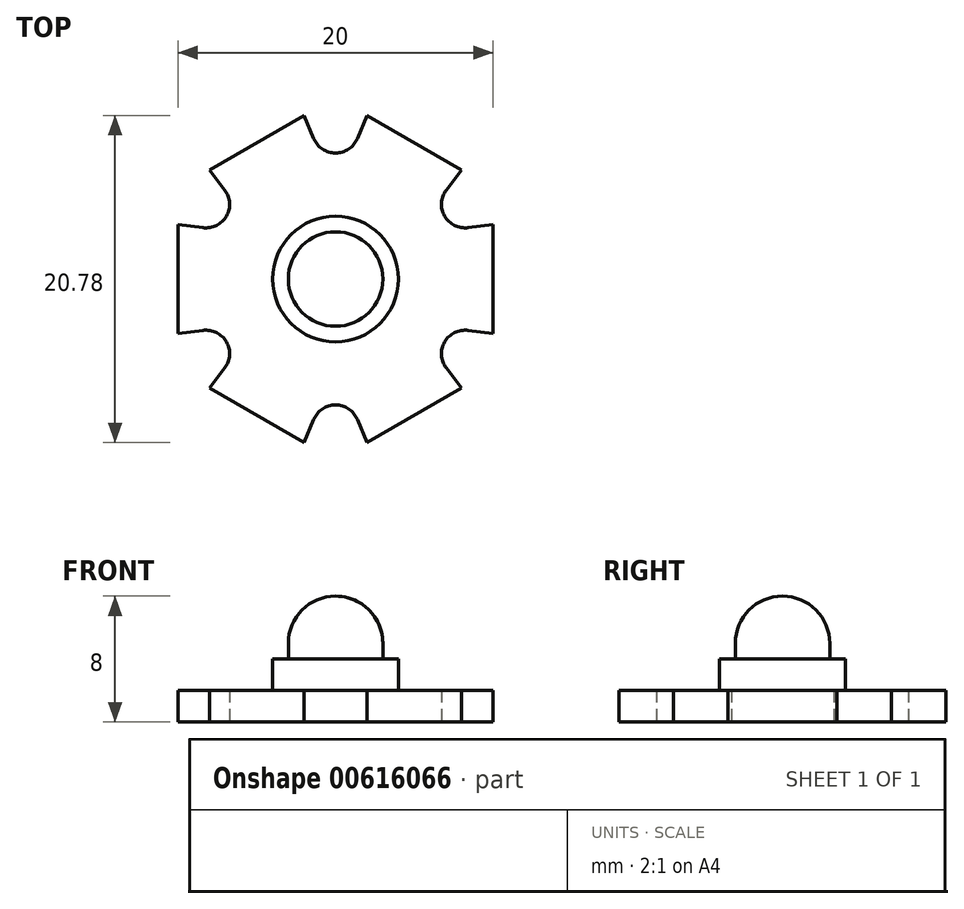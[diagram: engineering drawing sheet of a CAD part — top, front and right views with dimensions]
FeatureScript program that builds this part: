
annotation { "Feature Type Name" : "Feature", "Feature Type Description" : "" }
export const myFeature = defineFeature(function(context is Context, id is Id, definition is map)
    precondition{}
    {
        {
            var Q0;
            Q0=qCreatedBy(makeId("Top.planeOp"),FACE);
            var sketch = newSketch(context, id + "F0", { "sketchPlane" : qUnion([Q0])});
            skArc(sketch, "E0", {"start": v(0, -8) * mm, "mid": v(-0.83, -8.25) * mm, "end": v(-1.38, -8.92) * mm});
            skLineSegment(sketch, "E1", {"start": v(-1.38, -8.92) * mm, "end": v(-2, -10.4) * mm});
            skLineSegment(sketch, "E2", {"start": v(-2, -10.4) * mm, "end": v(-8, -6.93) * mm});
            skArc(sketch, "E3.MirrorCS", {"start": v(0, -8) * mm, "mid": v(0.83, -8.25) * mm, "end": v(1.38, -8.92) * mm});
            skLineSegment(sketch, "E4.MirrorCS", {"start": v(1.38, -8.92) * mm, "end": v(2, -10.4) * mm});
            skLineSegment(sketch, "E5.1.0", {"start": v(8, -6.93) * mm, "end": v(2, -10.4) * mm});
            skLineSegment(sketch, "E5.1.1", {"start": v(7.03, -5.66) * mm, "end": v(8, -6.93) * mm});
            skArc(sketch, "E5.1.2", {"start": v(6.93, -4) * mm, "mid": v(6.73, -4.85) * mm, "end": v(7.03, -5.66) * mm});
            skArc(sketch, "E5.1.3", {"start": v(6.93, -4) * mm, "mid": v(7.56, -3.4) * mm, "end": v(8.42, -3.26) * mm});
            skLineSegment(sketch, "E5.1.4", {"start": v(8.42, -3.26) * mm, "end": v(10, -3.46) * mm});
            skLineSegment(sketch, "E5.2.0", {"start": v(10, 3.46) * mm, "end": v(10, -3.46) * mm});
            skLineSegment(sketch, "E5.2.1", {"start": v(8.42, 3.26) * mm, "end": v(10, 3.46) * mm});
            skArc(sketch, "E5.2.2", {"start": v(6.93, 4) * mm, "mid": v(7.56, 3.4) * mm, "end": v(8.42, 3.26) * mm});
            skArc(sketch, "E5.2.3", {"start": v(6.93, 4) * mm, "mid": v(6.73, 4.85) * mm, "end": v(7.03, 5.66) * mm});
            skLineSegment(sketch, "E5.2.4", {"start": v(7.03, 5.66) * mm, "end": v(8, 6.93) * mm});
            skLineSegment(sketch, "E5.3.0", {"start": v(2, 10.4) * mm, "end": v(8, 6.93) * mm});
            skLineSegment(sketch, "E5.3.1", {"start": v(1.38, 8.92) * mm, "end": v(2, 10.4) * mm});
            skArc(sketch, "E5.3.2", {"start": v(0, 8) * mm, "mid": v(0.83, 8.25) * mm, "end": v(1.38, 8.92) * mm});
            skArc(sketch, "E5.3.3", {"start": v(0, 8) * mm, "mid": v(-0.83, 8.25) * mm, "end": v(-1.38, 8.92) * mm});
            skLineSegment(sketch, "E5.3.4", {"start": v(-1.38, 8.92) * mm, "end": v(-2, 10.4) * mm});
            skLineSegment(sketch, "E5.4.0", {"start": v(-8, 6.93) * mm, "end": v(-2, 10.4) * mm});
            skLineSegment(sketch, "E5.4.1", {"start": v(-7.03, 5.66) * mm, "end": v(-8, 6.93) * mm});
            skArc(sketch, "E5.4.2", {"start": v(-6.93, 4) * mm, "mid": v(-6.73, 4.85) * mm, "end": v(-7.03, 5.66) * mm});
            skArc(sketch, "E5.4.3", {"start": v(-6.93, 4) * mm, "mid": v(-7.56, 3.4) * mm, "end": v(-8.42, 3.26) * mm});
            skLineSegment(sketch, "E5.4.4", {"start": v(-8.42, 3.26) * mm, "end": v(-10, 3.46) * mm});
            skLineSegment(sketch, "E5.5.0", {"start": v(-10, -3.46) * mm, "end": v(-10, 3.46) * mm});
            skLineSegment(sketch, "E5.5.1", {"start": v(-8.42, -3.26) * mm, "end": v(-10, -3.46) * mm});
            skArc(sketch, "E5.5.2", {"start": v(-6.93, -4) * mm, "mid": v(-7.56, -3.4) * mm, "end": v(-8.42, -3.26) * mm});
            skArc(sketch, "E5.5.3", {"start": v(-6.93, -4) * mm, "mid": v(-6.73, -4.85) * mm, "end": v(-7.03, -5.66) * mm});
            skLineSegment(sketch, "E5.5.4", {"start": v(-7.03, -5.66) * mm, "end": v(-8, -6.93) * mm});
            skPoint(sketch, "E5.center", {"position": v(0, 0) * mm});
            skSolve(sketch);
        }
        {
            var Q0;
            Q0=makeQuery(id+"F0.imprint","IMPRINT",FACE,{"disambiguationData":[TD([[makeQuery(id+"F0.imprint","IMPRINT",EDGE,{"derivedFrom":sQuery(id+"F0.wireOp",EDGE,"E0")}),-1.0]])]});
            extrude(context, id + "F1", {"entities" : qUnion([Q0]), "depth" : 2 * mm, "offsetDistance" : 25 * mm});
        }
        {
            var Q0;
            Q0=makeQuery(id+"F1.opExtrude","CAP_FACE",FACE,{"disambiguationData":[OSD([sQuery(id+"F0.wireOp",EDGE,"E0"),sQuery(id+"F0.wireOp",EDGE,"E1"),sQuery(id+"F0.wireOp",EDGE,"E2"),sQuery(id+"F0.wireOp",EDGE,"E3.MirrorCS"),sQuery(id+"F0.wireOp",EDGE,"E4.MirrorCS"),sQuery(id+"F0.wireOp",EDGE,"E5.1.0"),sQuery(id+"F0.wireOp",EDGE,"E5.1.1"),sQuery(id+"F0.wireOp",EDGE,"E5.1.2"),sQuery(id+"F0.wireOp",EDGE,"E5.1.3"),sQuery(id+"F0.wireOp",EDGE,"E5.1.4"),sQuery(id+"F0.wireOp",EDGE,"E5.2.0"),sQuery(id+"F0.wireOp",EDGE,"E5.2.1"),sQuery(id+"F0.wireOp",EDGE,"E5.2.2"),sQuery(id+"F0.wireOp",EDGE,"E5.2.3"),sQuery(id+"F0.wireOp",EDGE,"E5.2.4"),sQuery(id+"F0.wireOp",EDGE,"E5.3.0"),sQuery(id+"F0.wireOp",EDGE,"E5.3.1"),sQuery(id+"F0.wireOp",EDGE,"E5.3.2"),sQuery(id+"F0.wireOp",EDGE,"E5.3.3"),sQuery(id+"F0.wireOp",EDGE,"E5.3.4"),sQuery(id+"F0.wireOp",EDGE,"E5.4.0"),sQuery(id+"F0.wireOp",EDGE,"E5.4.1"),sQuery(id+"F0.wireOp",EDGE,"E5.4.2"),sQuery(id+"F0.wireOp",EDGE,"E5.4.3"),sQuery(id+"F0.wireOp",EDGE,"E5.4.4"),sQuery(id+"F0.wireOp",EDGE,"E5.5.0"),sQuery(id+"F0.wireOp",EDGE,"E5.5.1"),sQuery(id+"F0.wireOp",EDGE,"E5.5.2"),sQuery(id+"F0.wireOp",EDGE,"E5.5.3"),sQuery(id+"F0.wireOp",EDGE,"E5.5.4")])],"isStart":false});
            var sketch = newSketch(context, id + "F2", { "sketchPlane" : qUnion([Q0])});
            skCircle(sketch, "E6", {"center": v(0, 0) * mm, "radius": 4 * mm});
            skSolve(sketch);
        }
        {
            var Q0;
            Q0 = qSketchRegion(id + "F2", true);
            extrude(context, id + "F3", {"entities" : qUnion([Q0]), "operationType" : NewBodyOperationType.ADD, "depth" : 2 * mm, "offsetDistance" : 25 * mm});
        }
        {
            var Q0;
            Q0=qCreatedBy(makeId("Front.planeOp"),FACE);
            var sketch = newSketch(context, id + "F4", { "sketchPlane" : qUnion([Q0])});
            skArc(sketch, "E7", {"start": v(3, 5) * mm, "mid": v(2.12, 7.12) * mm, "end": v(0, 8) * mm});
            skLineSegment(sketch, "E8", {"start": v(3, 5) * mm, "end": v(3, 4) * mm});
            skLineSegment(sketch, "E9", {"start": v(3, 4) * mm, "end": v(0, 4) * mm});
            skLineSegment(sketch, "E10", {"start": v(0, 4) * mm, "end": v(0, 8) * mm});
            skSolve(sketch);
        }
        {
            var Q0;
            Q0 = qSketchRegion(id + "F4", true);
            var Q1;
            Q1=sQuery(id+"F4.wireOp",EDGE,"E10");
            revolve(context, id + "F5", {"operationType" : NewBodyOperationType.ADD, "entities" : qUnion([Q0]), "axis" : qUnion([Q1]), "revolveType" : RevolveType.FULL});
        }
    });
